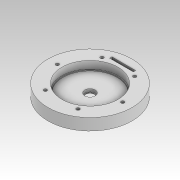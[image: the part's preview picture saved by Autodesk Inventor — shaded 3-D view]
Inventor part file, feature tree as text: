
AUTODESK INVENTOR PART (.ipt)
format: ipt  version: 2020 (Build 240168000, 168)  size: 248,832 bytes
history: native  units: mm
features: sketch x4, extrude x3, revolve x1, pattern_circular x1
ambient origin geometry x8: Origin, YZ Plane, XZ Plane, XY Plane, X Axis, Y Axis, Z Axis, Center Point
bodies: Body1 (feature_tree)
feature tree (9):
  revolve  "Revolution2"  [1 undecoded]
  extrude  "Extrusion18"  Depth=29.5mm
  extrude  "Extrusion19"  Depth=45.0mm
  pattern_circular  "Circular Pattern3"  [2 undecoded]
  extrude  "Extrusion20"  Depth=30.0mm
  sketch  "Sketch19"  dims[d90=0.5mm d91=5.6mm]
  sketch  "Sketch20"  dims[d92=1.0mm d93=29.5mm]
  sketch  "Sketch21"  dims[d94=40.5mm d95=45.0mm]
  sketch  "Sketch22"  dims[d96=1.0mm d97=1.0mm d99=30.0mm d100=1.0mm d101=8.0mm d102=90.0deg d103=3.0mm d104=70.0mm d105=3.5mm d106=0.0mm d107=0.0mm d108=5.8mm d109=5.8mm d110=3.0mm d111=0.0mm d112=60.0mm d113=360.0deg d115=35.0mm d116=25.4mm d117=2.54mm d118=10.0mm d119=0.0mm d64=0.5mm d65=0.872665mm d66=0.5mm d67=0.872665mm]
note: 3 required parameter values undecoded (feature->parameter linkage not recoverable at this tier; creation-order binding heuristic only, values carry confidence <= 0.55)